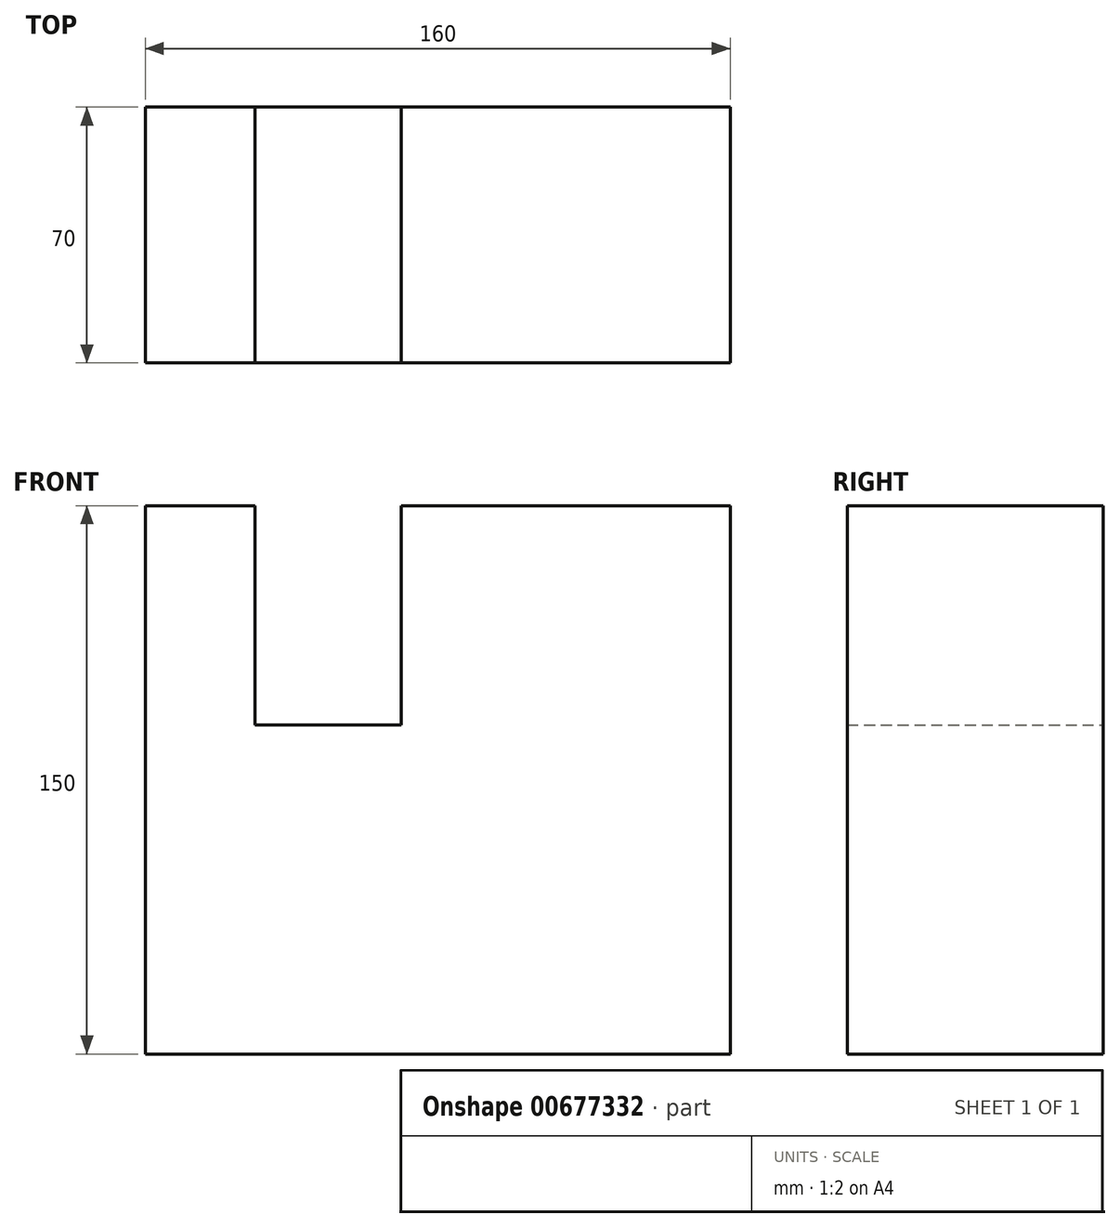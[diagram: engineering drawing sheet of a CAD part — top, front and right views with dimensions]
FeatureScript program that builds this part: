
annotation { "Feature Type Name" : "Feature", "Feature Type Description" : "" }
export const myFeature = defineFeature(function(context is Context, id is Id, definition is map)
    precondition{}
    {
        {
            var Q0;
            Q0=qCreatedBy(makeId("Front.planeOp"),FACE);
            var sketch = newSketch(context, id + "F0", { "sketchPlane" : qUnion([Q0])});
            skLineSegment(sketch, "E0", {"start": v(-80.85, 0) * mm, "end": v(79.15, 0) * mm});
            skLineSegment(sketch, "E1", {"start": v(79.15, 0) * mm, "end": v(79.15, 150) * mm});
            skLineSegment(sketch, "E2", {"start": v(79.15, 150) * mm, "end": v(-10.85, 150) * mm});
            skLineSegment(sketch, "E3", {"start": v(-10.85, 150) * mm, "end": v(-10.85, 90) * mm});
            skLineSegment(sketch, "E4", {"start": v(-10.85, 90) * mm, "end": v(-50.85, 90) * mm});
            skLineSegment(sketch, "E5", {"start": v(-50.85, 90) * mm, "end": v(-50.85, 150) * mm});
            skLineSegment(sketch, "E6", {"start": v(-50.85, 150) * mm, "end": v(-80.85, 150) * mm});
            skLineSegment(sketch, "E7", {"start": v(-80.85, 150) * mm, "end": v(-80.85, 0) * mm});
            skSolve(sketch);
        }
        {
            var Q0;
            Q0 = qSketchRegion(id + "F0", true);
            extrude(context, id + "F1", {"entities" : qUnion([Q0]), "depth" : 70 * mm, "offsetDistance" : 25 * mm});
        }
    });
